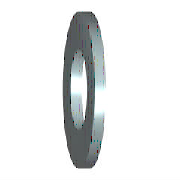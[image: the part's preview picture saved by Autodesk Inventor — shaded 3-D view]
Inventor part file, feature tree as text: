
AUTODESK INVENTOR PART (.ipt)
format: ipt  version: 2020 (Build 240168000, 168)  size: 110,080 bytes
history: native  units: mm (DEFAULTED — no unit token found)
features: other x1, plane x1, sketch x1
ambient origin geometry x7: Origin, YZ Plane, XY Plane, X Axis, Y Axis, Z Axis, Center Point
bodies: Solid1 (feature_tree), Body (feature_tree)
feature tree (3):
  other  "Work Axis1"
  plane  "Work Plane1"
  sketch  "Sketch"  dims[d0=5.3mm d1=10.0mm d2=1.0mm d3=0.0mm d4=0.0mm d5=0.0mm d6=0.0mm d7=0.0mm]
